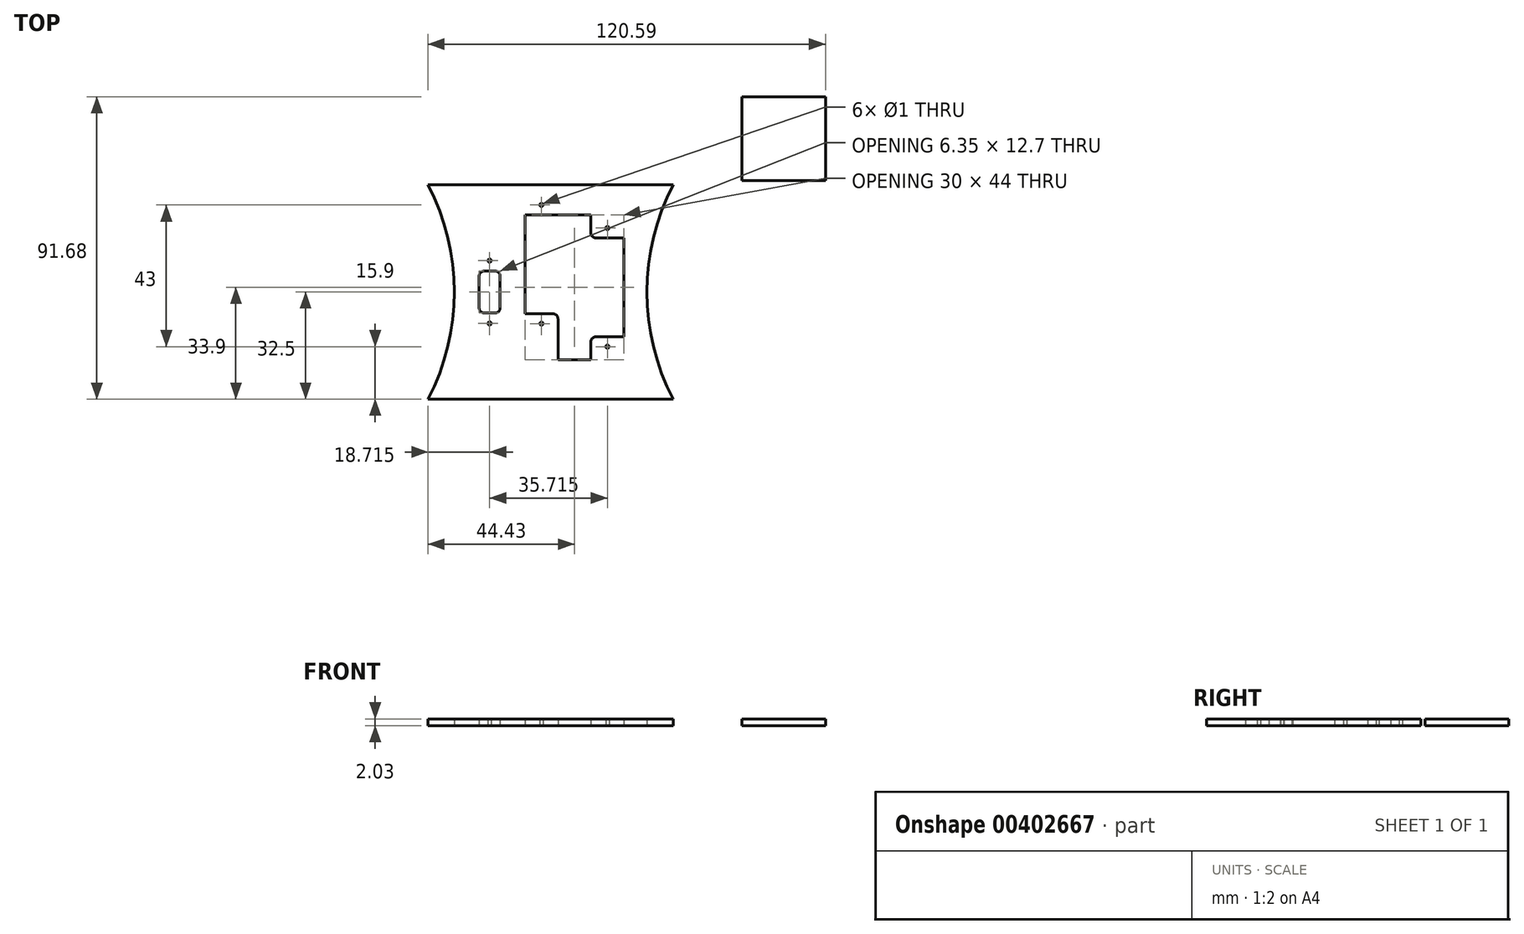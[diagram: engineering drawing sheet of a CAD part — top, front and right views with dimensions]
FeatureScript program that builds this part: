
annotation { "Feature Type Name" : "Feature", "Feature Type Description" : "" }
export const myFeature = defineFeature(function(context is Context, id is Id, definition is map)
    precondition{}
    {
        {
            var Q0;
            Q0=qCreatedBy(makeId("Top.planeOp"),FACE);
            var sketch = newSketch(context, id + "F0", { "sketchPlane" : qUnion([Q0])});
            skCircle(sketch, "E0", {"center": v(-35.71, -9.53) * mm, "radius": 0.5 * mm});
            skCircle(sketch, "E1.1.0.0", {"center": v(-35.71, 9.52) * mm, "radius": 0.5 * mm});
            skPoint(sketch, "E2.middle", {"position": v(-35.71, 0) * mm});
            skLineSegment(sketch, "E3.bottom", {"start": v(-30, 12.06) * mm, "end": v(-30, -12.07) * mm, "construction": true});
            skLineSegment(sketch, "E3.top", {"start": v(-41.43, 12.06) * mm, "end": v(-41.43, -12.07) * mm, "construction": true});
            skLineSegment(sketch, "E3.left", {"start": v(-30, 12.06) * mm, "end": v(-41.43, 12.06) * mm, "construction": true});
            skLineSegment(sketch, "E3.right", {"start": v(-30, -12.07) * mm, "end": v(-41.43, -12.07) * mm, "construction": true});
            skLineSegment(sketch, "E4.bottom", {"start": v(-32.54, -4.85) * mm, "end": v(-32.54, 4.85) * mm});
            skLineSegment(sketch, "E4.top", {"start": v(-38.89, -4.85) * mm, "end": v(-38.89, 4.85) * mm});
            skLineSegment(sketch, "E4.left", {"start": v(-34.04, -6.35) * mm, "end": v(-37.39, -6.35) * mm});
            skLineSegment(sketch, "E4.right", {"start": v(-34.04, 6.35) * mm, "end": v(-37.39, 6.35) * mm});
            skLineSegment(sketch, "E5", {"start": v(-32.54, 0) * mm, "end": v(-38.89, 0) * mm, "construction": true});
            skLineSegment(sketch, "E6", {"start": v(-35.71, 9.52) * mm, "end": v(-35.71, -9.53) * mm, "construction": true});
            skArc(sketch, "E7.filletArc", {"start": v(-32.54, 4.85) * mm, "mid": v(-32.98, 5.91) * mm, "end": v(-34.04, 6.35) * mm});
            skPoint(sketch, "E8.visualSharp", {"position": v(-38.89, 6.35) * mm});
            skArc(sketch, "E8.filletArc", {"start": v(-37.39, 6.35) * mm, "mid": v(-38.45, 5.91) * mm, "end": v(-38.89, 4.85) * mm});
            skPoint(sketch, "E9.visualSharp", {"position": v(-38.89, -6.35) * mm});
            skArc(sketch, "E9.filletArc", {"start": v(-38.89, -4.85) * mm, "mid": v(-38.45, -5.91) * mm, "end": v(-37.39, -6.35) * mm});
            skPoint(sketch, "E10.visualSharp", {"position": v(-32.54, -6.35) * mm});
            skArc(sketch, "E10.filletArc", {"start": v(-34.04, -6.35) * mm, "mid": v(-32.98, -5.91) * mm, "end": v(-32.54, -4.85) * mm});
            skCircle(sketch, "E11", {"center": v(0, 19.4) * mm, "radius": 0.5 * mm});
            skLineSegment(sketch, "E12", {"start": v(-46.43, 0) * mm, "end": v(12, 0) * mm, "construction": true});
            skPoint(sketch, "E13.MirrorP", {"position": v(-20, -9.6) * mm});
            skPoint(sketch, "E14.orphan", {"position": v(12, 0) * mm});
            skLineSegment(sketch, "E15", {"start": v(-46.43, 0) * mm, "end": v(-46.43, 32.5) * mm, "construction": true});
            skLineSegment(sketch, "E16.MirrorCS", {"start": v(-46.43, 0) * mm, "end": v(-46.43, -32.5) * mm, "construction": true});
            skCircle(sketch, "E17", {"center": v(-20, -9.6) * mm, "radius": 0.5 * mm});
            skArc(sketch, "E18", {"start": v(-54.43, -32.5) * mm, "mid": v(-46.43, 0) * mm, "end": v(-54.43, 32.5) * mm});
            skLineSegment(sketch, "E19", {"start": v(-54.43, -32.5) * mm, "end": v(20, -32.5) * mm});
            skLineSegment(sketch, "E20", {"start": v(12, -32.5) * mm, "end": v(12, 32.5) * mm, "construction": true});
            skLineSegment(sketch, "E21", {"start": v(-54.43, 32.5) * mm, "end": v(20, 32.5) * mm});
            skPoint(sketch, "E22", {"position": v(-35.71, -12.07) * mm});
            skArc(sketch, "E23", {"start": v(20, 32.5) * mm, "mid": v(12, 0) * mm, "end": v(20, -32.5) * mm});
            skLineSegment(sketch, "E24", {"start": v(-15, -20.6) * mm, "end": v(-5, -20.6) * mm});
            skLineSegment(sketch, "E25", {"start": v(-5, -20.6) * mm, "end": v(-5, -15.1) * mm});
            skLineSegment(sketch, "E26.bottom", {"start": v(40.76, 59.18) * mm, "end": v(66.16, 59.18) * mm});
            skLineSegment(sketch, "E26.top", {"start": v(40.76, 33.78) * mm, "end": v(66.16, 33.78) * mm});
            skLineSegment(sketch, "E26.left", {"start": v(40.76, 59.18) * mm, "end": v(40.76, 33.78) * mm});
            skLineSegment(sketch, "E26.right", {"start": v(66.16, 59.18) * mm, "end": v(66.16, 33.78) * mm});
            skLineSegment(sketch, "E27", {"start": v(-10, -20.6) * mm, "end": v(-10, 23.4) * mm, "construction": true});
            skLineSegment(sketch, "E28.MirrorCS", {"start": v(-25, 23.4) * mm, "end": v(-25, -6.6) * mm});
            skLineSegment(sketch, "E29.MirrorCS", {"start": v(-25, -6.6) * mm, "end": v(-16.5, -6.6) * mm});
            skLineSegment(sketch, "E30.MirrorCS", {"start": v(-15, -20.6) * mm, "end": v(-15, -8.1) * mm});
            skLineSegment(sketch, "E31.MirrorCS", {"start": v(5, -13.6) * mm, "end": v(-3.5, -13.6) * mm});
            skLineSegment(sketch, "E32.MirrorCS", {"start": v(5, 16.4) * mm, "end": v(5, -13.6) * mm});
            skCircle(sketch, "E33.MirrorC", {"center": v(-20, 0) * mm, "radius": 2.5 * mm, "construction": true});
            skCircle(sketch, "E34.MirrorC", {"center": v(0, -7) * mm, "radius": 2.5 * mm, "construction": true});
            skCircle(sketch, "E35.MirrorC", {"center": v(-20, 26.4) * mm, "radius": 0.5 * mm});
            skCircle(sketch, "E36.MirrorC", {"center": v(0, -16.6) * mm, "radius": 0.5 * mm});
            skPoint(sketch, "E37.orphan", {"position": v(-15, -20.6) * mm});
            skLineSegment(sketch, "E38", {"start": v(-25, 23.4) * mm, "end": v(-5, 23.4) * mm});
            skLineSegment(sketch, "E39", {"start": v(-5, 23.4) * mm, "end": v(-5, 17.9) * mm});
            skLineSegment(sketch, "E40", {"start": v(-3.5, 16.4) * mm, "end": v(5, 16.4) * mm});
            skArc(sketch, "E41.filletArc", {"start": v(-5, 17.9) * mm, "mid": v(-4.56, 16.84) * mm, "end": v(-3.5, 16.4) * mm});
            skArc(sketch, "E42.filletArc", {"start": v(-15, -8.1) * mm, "mid": v(-15.44, -7.04) * mm, "end": v(-16.5, -6.6) * mm});
            skArc(sketch, "E43.filletArc", {"start": v(-3.5, -13.6) * mm, "mid": v(-4.56, -14.04) * mm, "end": v(-5, -15.1) * mm});
            skSolve(sketch);
        }
        {
            var Q0;
            Q0=qSketchRegion(id+"F0",true);
            extrude(context, id + "F1", {"entities" : qUnion([Q0]), "depth" : 2.03 * mm});
        }
    });
